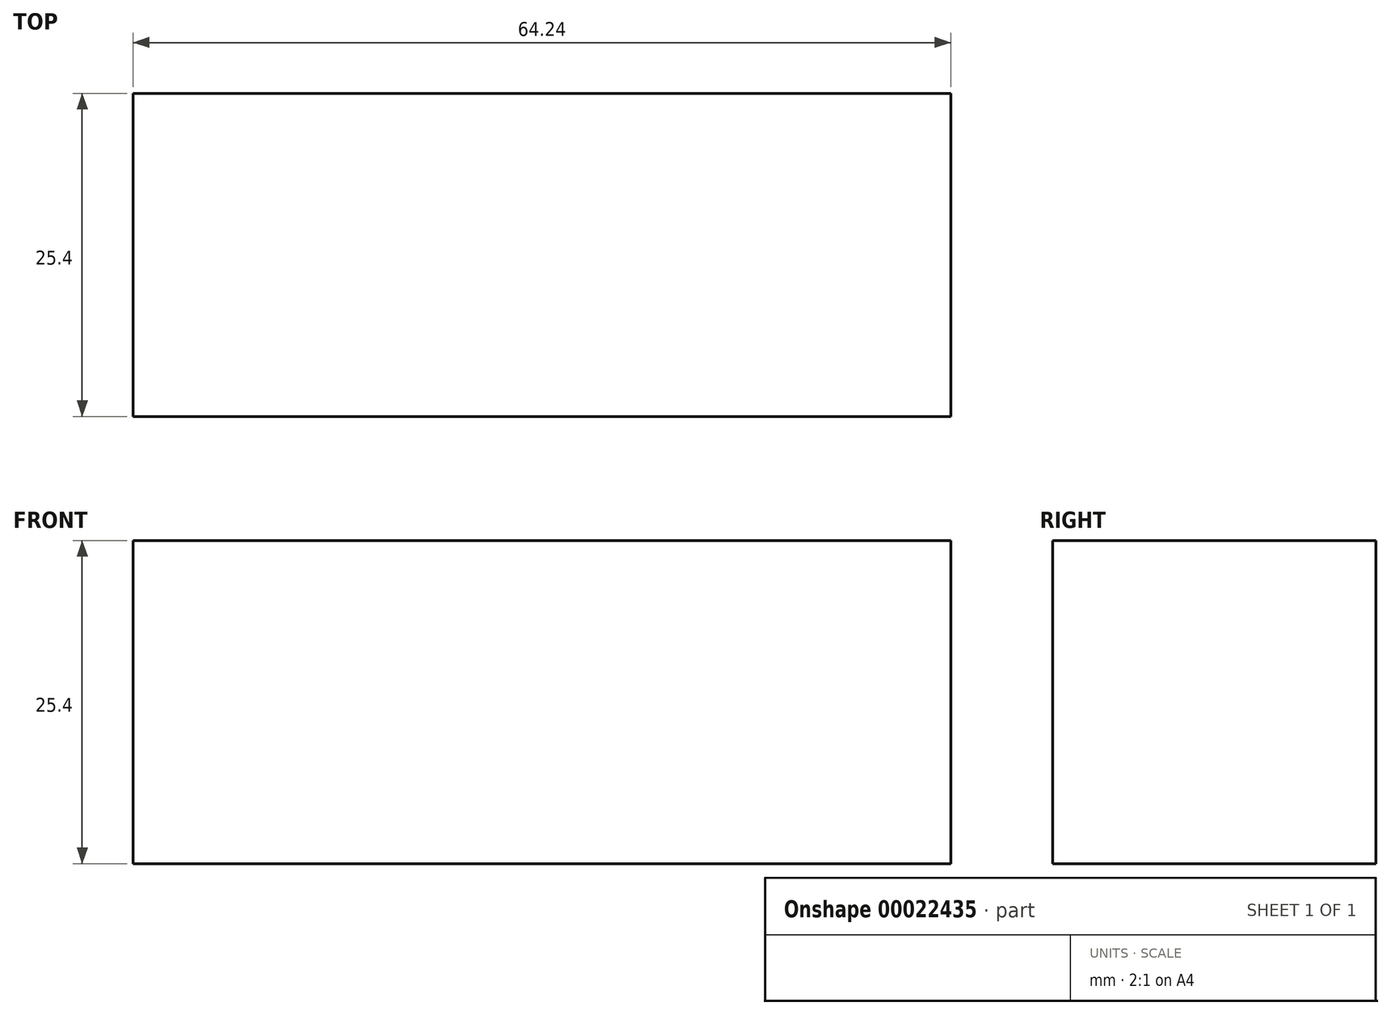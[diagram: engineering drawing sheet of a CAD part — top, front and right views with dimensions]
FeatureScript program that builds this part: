
annotation { "Feature Type Name" : "Feature", "Feature Type Description" : "" }
export const myFeature = defineFeature(function(context is Context, id is Id, definition is map)
    precondition{}
    {
        {
            var Q0;
            Q0=qCreatedBy(makeId("Top.planeOp"),FACE);
            var sketch = newSketch(context, id + "F0", { "sketchPlane" : qUnion([Q0])});
            skLineSegment(sketch, "E0.bottom", {"start": v(0, 0) * mm, "end": v(64.24, 0) * mm});
            skLineSegment(sketch, "E0.top", {"start": v(0, 25.4) * mm, "end": v(64.24, 25.4) * mm});
            skLineSegment(sketch, "E0.left", {"start": v(0, 0) * mm, "end": v(0, 25.4) * mm});
            skLineSegment(sketch, "E0.right", {"start": v(64.24, 0) * mm, "end": v(64.24, 25.4) * mm});
            skSolve(sketch);
        }
        {
            var Q0;
            Q0=makeQuery(id+"F0.imprint","IMPRINT",FACE,{"disambiguationData":[TD([[makeQuery(id+"F0.imprint","IMPRINT",EDGE,{"derivedFrom":sQuery(id+"F0.wireOp",EDGE,"E0.bottom")}),1.0]])]});
            extrude(context, id + "F1", {"entities" : qUnion([Q0]), "depth" : 25.4 * mm});
        }
    });
